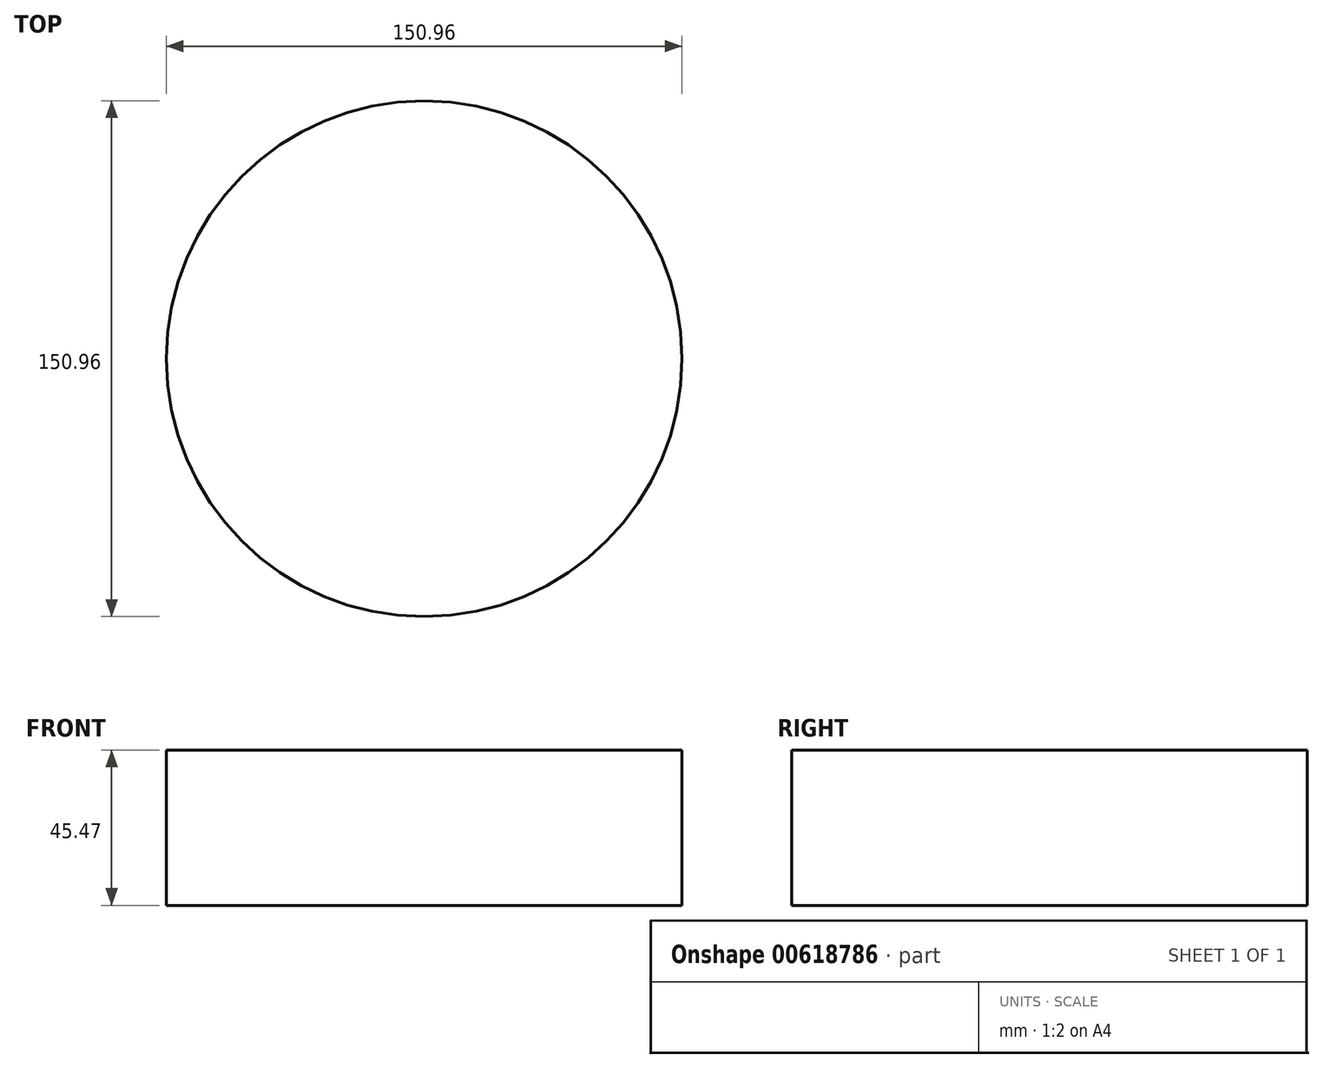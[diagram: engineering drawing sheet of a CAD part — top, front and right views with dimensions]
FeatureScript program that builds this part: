
annotation { "Feature Type Name" : "Feature", "Feature Type Description" : "" }
export const myFeature = defineFeature(function(context is Context, id is Id, definition is map)
    precondition{}
    {
        {
            var Q0;
            Q0=qCreatedBy(makeId("Top.planeOp"),FACE);
            var sketch = newSketch(context, id + "F0", { "sketchPlane" : qUnion([Q0])});
            skCircle(sketch, "E0", {"center": v(0, 0) * mm, "radius": 75.48 * mm});
            skSolve(sketch);
        }
        {
            var Q0;
            Q0 = qSketchRegion(id + "F0", true);
            extrude(context, id + "F1", {"entities" : qUnion([Q0]), "depth" : 45.47 * mm, "offsetDistance" : 25.4 * mm});
        }
    });
